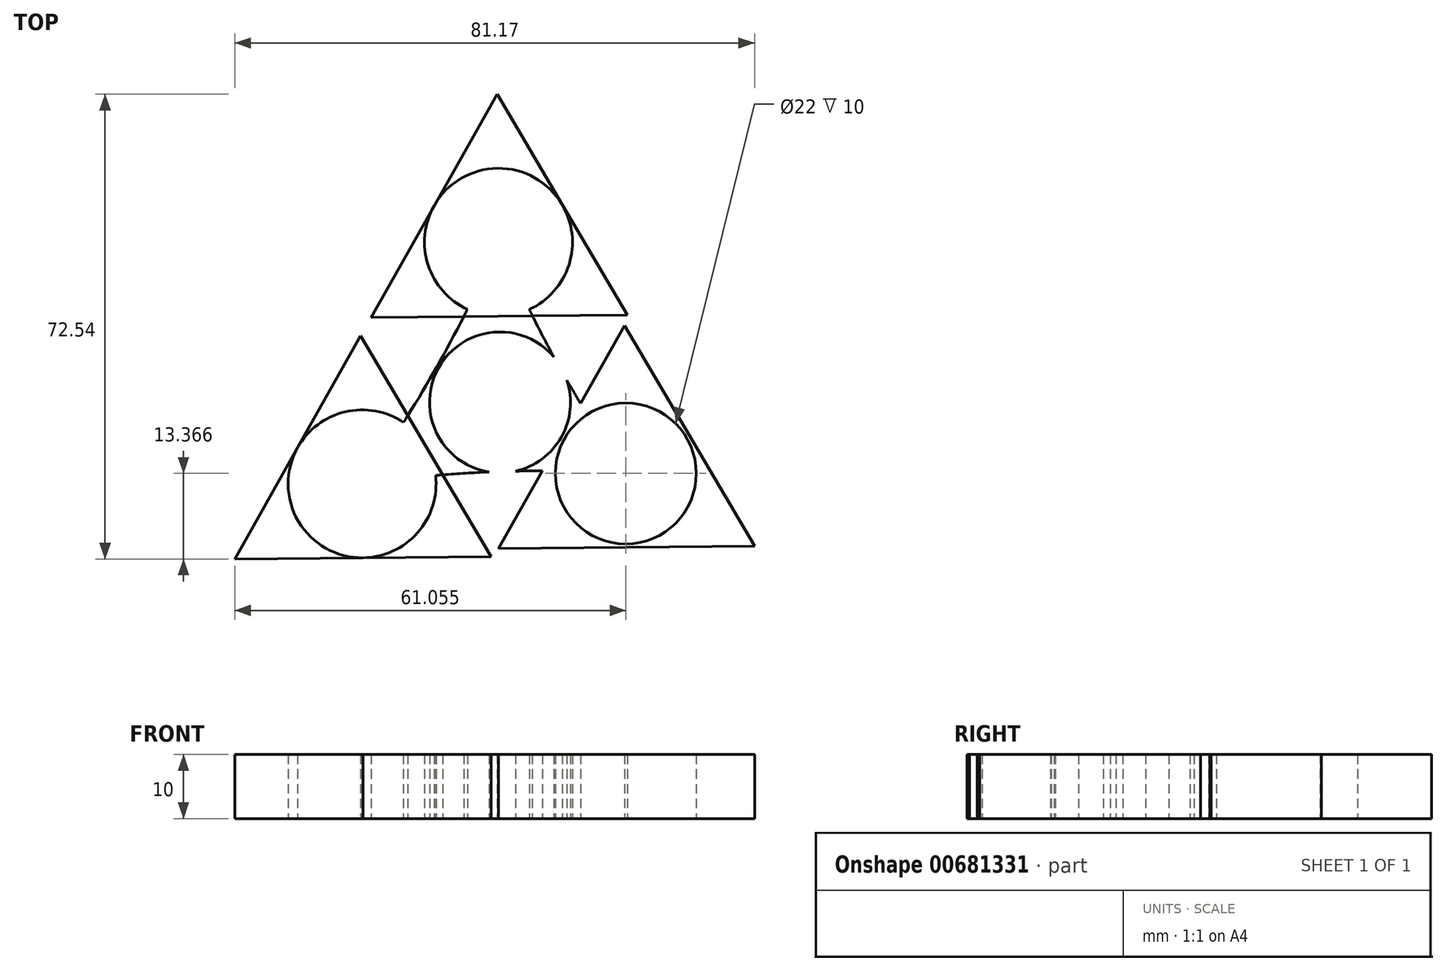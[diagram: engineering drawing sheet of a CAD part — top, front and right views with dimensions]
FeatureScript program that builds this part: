
annotation { "Feature Type Name" : "Feature", "Feature Type Description" : "" }
export const myFeature = defineFeature(function(context is Context, id is Id, definition is map)
    precondition{}
    {
        {
            var Q0;
            Q0=qCreatedBy(makeId("Top.planeOp"),FACE);
            var sketch = newSketch(context, id + "F0", { "sketchPlane" : qUnion([Q0])});
            skPoint(sketch, "E0.0.midPoint", {"position": v(22.1, 13.05) * mm});
            skLineSegment(sketch, "E1", {"start": v(0, 0) * mm, "end": v(-0.49, 50) * mm});
            skLineSegment(sketch, "E2", {"start": v(0, 0) * mm, "end": v(39.27, -22.17) * mm});
            skLineSegment(sketch, "E3", {"start": v(0, 0) * mm, "end": v(-43.06, -25.42) * mm});
            skCircle(sketch, "E4", {"center": v(-21.53, -12.7) * mm, "radius": 11.55 * mm});
            skCircle(sketch, "E5", {"center": v(19.63, -11.08) * mm, "radius": 11 * mm});
            skCircle(sketch, "E6", {"center": v(-0.24, 25) * mm, "radius": 11.55 * mm});
            skCircle(sketch, "E7", {"center": v(0, 0) * mm, "radius": 11 * mm});
            skPoint(sketch, "E8", {"position": v(29.21, -16.5) * mm});
            skArc(sketch, "E9", {"start": v(-21.53, -12.7) * mm, "mid": v(-9.86, 5.57) * mm, "end": v(-0.24, 25) * mm});
            skArc(sketch, "E10", {"start": v(-0.24, 25) * mm, "mid": v(8.76, 6.44) * mm, "end": v(19.63, -11.08) * mm});
            skArc(sketch, "E11", {"start": v(19.63, -11.08) * mm, "mid": v(-0.99, -10.83) * mm, "end": v(-21.53, -12.7) * mm});
            skCircle(sketch, "E12.cCircle", {"center": v(-0.24, 25) * mm, "radius": 11.55 * mm, "construction": true});
            skPoint(sketch, "E12.0.midPoint", {"position": v(-0.35, 36.55) * mm});
            skCircle(sketch, "E13.cCircle", {"center": v(-21.53, -12.7) * mm, "radius": 11.55 * mm, "construction": true});
            skLineSegment(sketch, "E13.0", {"start": v(-21.75, 10.38) * mm, "end": v(-1.42, -24.06) * mm});
            skLineSegment(sketch, "E13.1", {"start": v(-1.42, -24.06) * mm, "end": v(-41.42, -24.45) * mm});
            skLineSegment(sketch, "E13.2", {"start": v(-41.42, -24.45) * mm, "end": v(-21.75, 10.38) * mm});
            skPoint(sketch, "E13.0.midPoint", {"position": v(-11.58, -6.84) * mm});
            skLineSegment(sketch, "E14.0", {"start": v(19.87, 13.65) * mm, "end": v(-20.13, 13.26) * mm});
            skLineSegment(sketch, "E14.1", {"start": v(-20.13, 13.26) * mm, "end": v(-0.47, 48.1) * mm});
            skLineSegment(sketch, "E14.2", {"start": v(-0.47, 48.1) * mm, "end": v(19.87, 13.65) * mm});
            skPoint(sketch, "E14.0.midPoint", {"position": v(-0.13, 13.45) * mm});
            skCircle(sketch, "E15.cCircle", {"center": v(19.63, -11.08) * mm, "radius": 11.55 * mm, "construction": true});
            skLineSegment(sketch, "E15.0", {"start": v(-0.25, -22.82) * mm, "end": v(19.41, 12) * mm});
            skLineSegment(sketch, "E15.1", {"start": v(19.41, 12) * mm, "end": v(39.75, -22.44) * mm});
            skLineSegment(sketch, "E15.2", {"start": v(39.75, -22.44) * mm, "end": v(-0.25, -22.82) * mm});
            skPoint(sketch, "E15.0.midPoint", {"position": v(9.58, -5.4) * mm});
            skSolve(sketch);
        }
        {
            var Q0;
            {var subQ0=sQuery(id+"F0.wireOp",EDGE,"E13.2");var subQ1=sQuery(id+"F0.wireOp",EDGE,"E4");var subQ2=makeQuery(id+"F0.imprint","INTERSECT",VERTEX,{"derivedFrom":[subQ1,subQ0]});Q0=makeQuery(id+"F0.imprint","IMPRINT",FACE,{"disambiguationData":[TD([[makeQuery(id+"F0.imprint","IMPRINT",EDGE,{"disambiguationData":[TD([[subQ2,1.0]])],"derivedFrom":subQ1}),-1.0]])]});}
            var Q1;
            {var subQ0=sQuery(id+"F0.wireOp",EDGE,"E13.2");var subQ3=sQuery(id+"F0.wireOp",EDGE,"E4");var subQ5=makeQuery(id+"F0.imprint","INTERSECT",VERTEX,{"derivedFrom":[subQ3,subQ0]});Q1=makeQuery(id+"F0.imprint","IMPRINT",FACE,{"disambiguationData":[TD([[makeQuery(id+"F0.imprint","IMPRINT",EDGE,{"disambiguationData":[TD([[subQ5,-1.0]])],"derivedFrom":subQ3}),-1.0]])]});}
            var Q2;
            {var subQ0=sQuery(id+"F0.wireOp",EDGE,"E13.1");var subQ1=sQuery(id+"F0.wireOp",EDGE,"E4");var subQ2=makeQuery(id+"F0.imprint","INTERSECT",VERTEX,{"derivedFrom":[subQ1,subQ0]});Q2=makeQuery(id+"F0.imprint","IMPRINT",FACE,{"disambiguationData":[TD([[makeQuery(id+"F0.imprint","IMPRINT",EDGE,{"disambiguationData":[TD([[subQ2,-1.0]])],"derivedFrom":subQ1}),-1.0]])]});}
            var Q3;
            {var subQ0=sQuery(id+"F0.wireOp",EDGE,"E13.1");var subQ3=sQuery(id+"F0.wireOp",EDGE,"E4");var subQ5=makeQuery(id+"F0.imprint","INTERSECT",VERTEX,{"derivedFrom":[subQ3,subQ0]});Q3=makeQuery(id+"F0.imprint","IMPRINT",FACE,{"disambiguationData":[TD([[makeQuery(id+"F0.imprint","IMPRINT",EDGE,{"disambiguationData":[TD([[subQ5,1.0]])],"derivedFrom":subQ3}),-1.0]])]});}
            var Q4;
            {var subQ5=sQuery(id+"F0.wireOp",EDGE,"E7");var subQ6=sQuery(id+"F0.wireOp",EDGE,"E1");var subQ7=makeQuery(id+"F0.imprint","INTERSECT",VERTEX,{"derivedFrom":[subQ6,subQ5]});Q4=makeQuery(id+"F0.imprint","IMPRINT",FACE,{"disambiguationData":[TD([[makeQuery(id+"F0.imprint","IMPRINT",EDGE,{"disambiguationData":[TD([[subQ7,-1.0]])],"derivedFrom":subQ5}),-1.0]])]});}
            var Q5;
            {var subQ0=sQuery(id+"F0.wireOp",EDGE,"E7");var subQ5=sQuery(id+"F0.wireOp",EDGE,"E10");var subQ6=makeQuery(id+"F0.imprint","INTERSECT",VERTEX,{"disambiguationData":[OD(0.0)],"derivedFrom":[subQ0,subQ5]});Q5=makeQuery(id+"F0.imprint","IMPRINT",FACE,{"disambiguationData":[TD([[makeQuery(id+"F0.imprint","IMPRINT",EDGE,{"disambiguationData":[TD([[subQ6,-1.0]])],"derivedFrom":subQ0}),-1.0]])]});}
            var Q6;
            {var subQ0=sQuery(id+"F0.wireOp",EDGE,"E5");var subQ1=sQuery(id+"F0.wireOp",EDGE,"E2");var subQ2=makeQuery(id+"F0.imprint","INTERSECT",VERTEX,{"disambiguationData":[OD(1.0)],"derivedFrom":[subQ1,subQ0]});Q6=makeQuery(id+"F0.imprint","IMPRINT",FACE,{"disambiguationData":[TD([[makeQuery(id+"F0.imprint","IMPRINT",EDGE,{"disambiguationData":[TD([[subQ2,1.0]])],"derivedFrom":subQ0}),-1.0]])]});}
            var Q7;
            {var subQ0=sQuery(id+"F0.wireOp",EDGE,"E10");var subQ1=sQuery(id+"F0.wireOp",EDGE,"E7");var subQ2=makeQuery(id+"F0.imprint","INTERSECT",VERTEX,{"disambiguationData":[OD(1.0)],"derivedFrom":[subQ1,subQ0]});Q7=makeQuery(id+"F0.imprint","IMPRINT",FACE,{"disambiguationData":[TD([[makeQuery(id+"F0.imprint","IMPRINT",EDGE,{"disambiguationData":[TD([[subQ2,-1.0]])],"derivedFrom":subQ0}),-1.0]])]});}
            var Q8;
            {var subQ10=sQuery(id+"F0.wireOp",EDGE,"E15.1");Q8=makeQuery(id+"F0.imprint","IMPRINT",FACE,{"disambiguationData":[TD([[makeQuery(id+"F0.imprint","IMPRINT",EDGE,{"derivedFrom":subQ10}),-1.0]])]});}
            var Q9;
            {var subQ0=sQuery(id+"F0.wireOp",EDGE,"E7");var subQ5=sQuery(id+"F0.wireOp",EDGE,"E11");var subQ6=makeQuery(id+"F0.imprint","INTERSECT",VERTEX,{"disambiguationData":[OD(0.0)],"derivedFrom":[subQ0,subQ5]});Q9=makeQuery(id+"F0.imprint","IMPRINT",FACE,{"disambiguationData":[TD([[makeQuery(id+"F0.imprint","IMPRINT",EDGE,{"disambiguationData":[TD([[subQ6,1.0]])],"derivedFrom":subQ0}),-1.0]])]});}
            var Q10;
            {var subQ0=sQuery(id+"F0.wireOp",EDGE,"E5");var subQ1=sQuery(id+"F0.wireOp",EDGE,"E2");var subQ2=makeQuery(id+"F0.imprint","INTERSECT",VERTEX,{"disambiguationData":[OD(1.0)],"derivedFrom":[subQ1,subQ0]});Q10=makeQuery(id+"F0.imprint","IMPRINT",FACE,{"disambiguationData":[TD([[makeQuery(id+"F0.imprint","IMPRINT",EDGE,{"disambiguationData":[TD([[subQ2,-1.0]])],"derivedFrom":subQ0}),-1.0]])]});}
            var Q11;
            {var subQ0=sQuery(id+"F0.wireOp",EDGE,"E11");var subQ1=sQuery(id+"F0.wireOp",EDGE,"E7");var subQ2=makeQuery(id+"F0.imprint","INTERSECT",VERTEX,{"disambiguationData":[OD(1.0)],"derivedFrom":[subQ1,subQ0]});Q11=makeQuery(id+"F0.imprint","IMPRINT",FACE,{"disambiguationData":[TD([[makeQuery(id+"F0.imprint","IMPRINT",EDGE,{"disambiguationData":[TD([[subQ2,1.0]])],"derivedFrom":subQ0}),-1.0]])]});}
            var Q12;
            {var subQ0=sQuery(id+"F0.wireOp",EDGE,"E14.1");var subQ1=sQuery(id+"F0.wireOp",EDGE,"E6");var subQ2=makeQuery(id+"F0.imprint","INTERSECT",VERTEX,{"derivedFrom":[subQ1,subQ0]});Q12=makeQuery(id+"F0.imprint","IMPRINT",FACE,{"disambiguationData":[TD([[makeQuery(id+"F0.imprint","IMPRINT",EDGE,{"disambiguationData":[TD([[subQ2,-1.0]])],"derivedFrom":subQ1}),-1.0]])]});}
            var Q13;
            {var subQ0=sQuery(id+"F0.wireOp",EDGE,"E14.1");var subQ3=sQuery(id+"F0.wireOp",EDGE,"E6");var subQ5=makeQuery(id+"F0.imprint","INTERSECT",VERTEX,{"derivedFrom":[subQ3,subQ0]});Q13=makeQuery(id+"F0.imprint","IMPRINT",FACE,{"disambiguationData":[TD([[makeQuery(id+"F0.imprint","IMPRINT",EDGE,{"disambiguationData":[TD([[subQ5,1.0]])],"derivedFrom":subQ3}),-1.0]])]});}
            var Q14;
            {var subQ0=sQuery(id+"F0.wireOp",EDGE,"E14.2");var subQ3=sQuery(id+"F0.wireOp",EDGE,"E6");var subQ5=makeQuery(id+"F0.imprint","INTERSECT",VERTEX,{"derivedFrom":[subQ3,subQ0]});Q14=makeQuery(id+"F0.imprint","IMPRINT",FACE,{"disambiguationData":[TD([[makeQuery(id+"F0.imprint","IMPRINT",EDGE,{"disambiguationData":[TD([[subQ5,-1.0]])],"derivedFrom":subQ3}),-1.0]])]});}
            var Q15;
            {var subQ0=sQuery(id+"F0.wireOp",EDGE,"E14.2");var subQ1=sQuery(id+"F0.wireOp",EDGE,"E6");var subQ2=makeQuery(id+"F0.imprint","INTERSECT",VERTEX,{"derivedFrom":[subQ1,subQ0]});Q15=makeQuery(id+"F0.imprint","IMPRINT",FACE,{"disambiguationData":[TD([[makeQuery(id+"F0.imprint","IMPRINT",EDGE,{"disambiguationData":[TD([[subQ2,1.0]])],"derivedFrom":subQ1}),-1.0]])]});}
            extrude(context, id + "F1", {"entities" : qUnion([Q0, Q1, Q2, Q3, Q4, Q5, Q6, Q7, Q8, Q9, Q10, Q11, Q12, Q13, Q14, Q15]), "depth" : 10 * mm, "offsetDistance" : 25 * mm});
        }
    });
